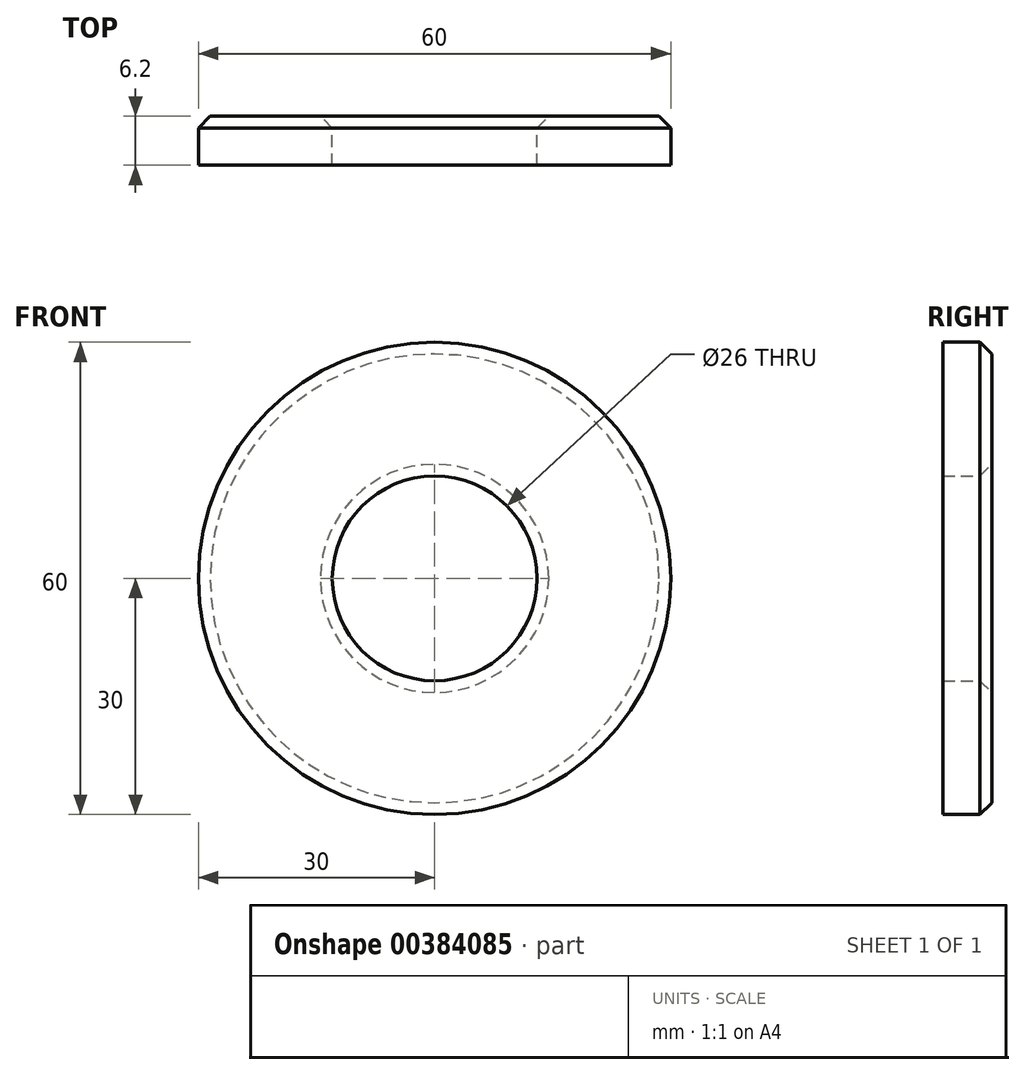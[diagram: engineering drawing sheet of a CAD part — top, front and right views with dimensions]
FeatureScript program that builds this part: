
annotation { "Feature Type Name" : "Feature", "Feature Type Description" : "" }
export const myFeature = defineFeature(function(context is Context, id is Id, definition is map)
    precondition{}
    {
        {
            var Q0;
            Q0=qCreatedBy(makeId("Front.planeOp"),FACE);
            var sketch = newSketch(context, id + "F0", { "sketchPlane" : qUnion([Q0])});
            skCircle(sketch, "E0", {"center": v(0, 0) * mm, "radius": 13 * mm});
            skCircle(sketch, "E1", {"center": v(0, 0) * mm, "radius": 30 * mm});
            skSolve(sketch);
        }
        {
            var Q0;
            Q0 = qSketchRegion(id + "F0", true);
            extrude(context, id + "F1", {"entities" : qUnion([Q0]), "depth" : 6.2 * mm});
        }
        {
            var Q0;
            Q0=makeQuery(id+"F1.opExtrude","CAP_EDGE",EDGE,{"disambiguationData":[OSD([sQuery(id+"F0.wireOp",EDGE,"E0")])],"isStart":true});
            var Q1;
            Q1=makeQuery(id+"F1.opExtrude","CAP_EDGE",EDGE,{"disambiguationData":[OSD([sQuery(id+"F0.wireOp",EDGE,"E1")])],"isStart":true});
            chamfer(context, id + "F2", {"entities" : qUnion([Q0, Q1]), "width" : 1.5 * mm, "tangentPropagation" : true});
        }
    });
